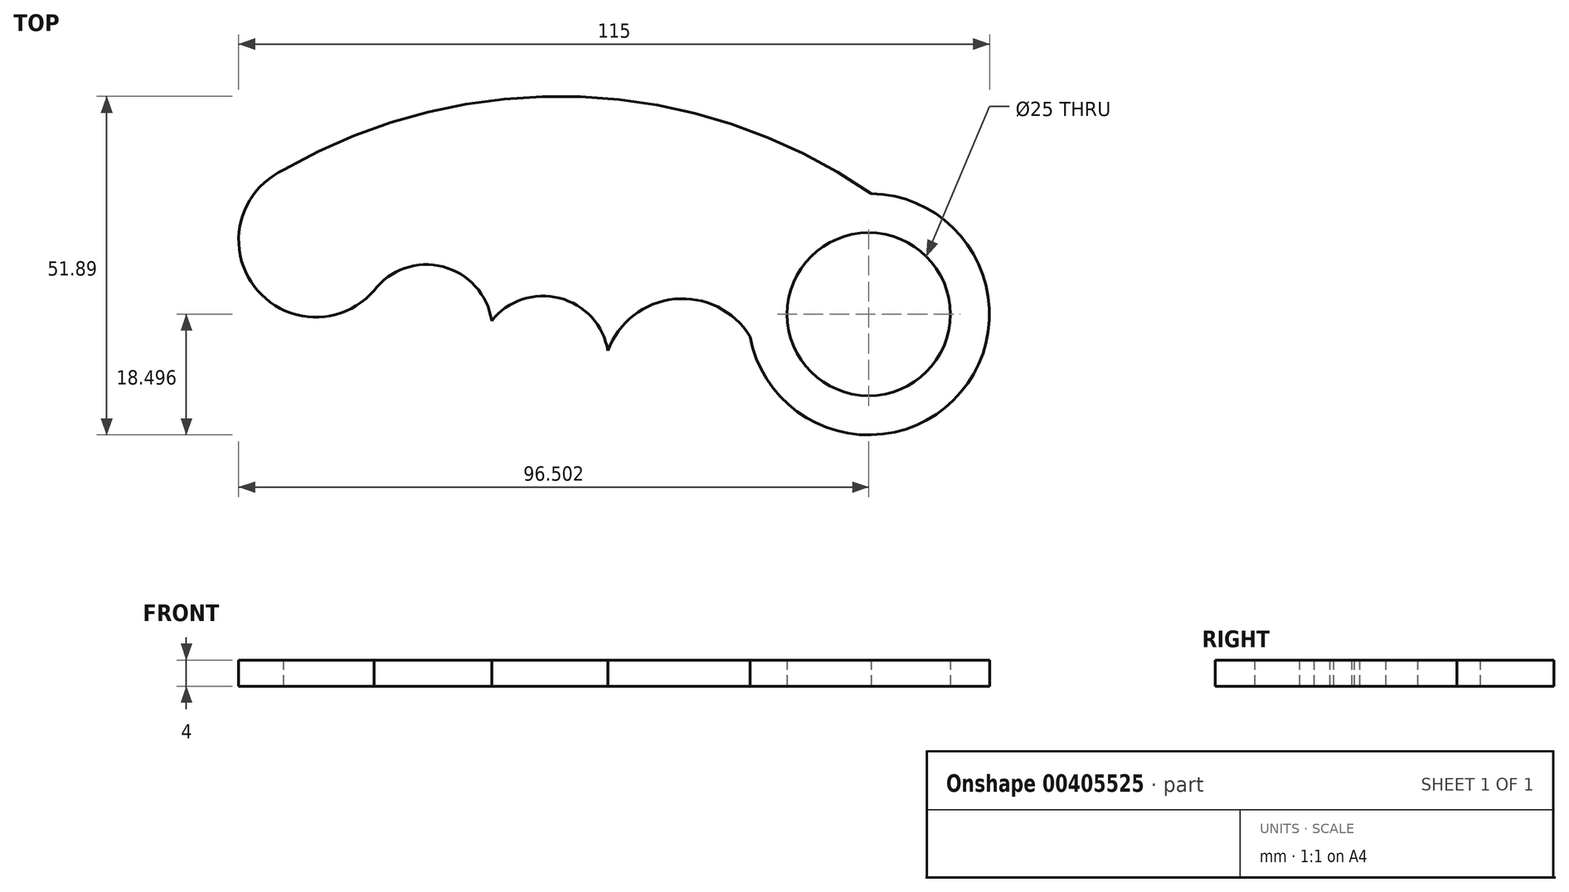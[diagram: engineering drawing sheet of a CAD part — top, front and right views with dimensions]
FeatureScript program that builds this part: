
annotation { "Feature Type Name" : "Feature", "Feature Type Description" : "" }
export const myFeature = defineFeature(function(context is Context, id is Id, definition is map)
    precondition{}
    {
        {
            var Q0;
            Q0=qCreatedBy(makeId("Top.planeOp"),FACE);
            var sketch = newSketch(context, id + "F0", { "sketchPlane" : qUnion([Q0])});
            skCircle(sketch, "E0", {"center": v(47.5, -8.81) * mm, "radius": 12.5 * mm});
            skCircle(sketch, "E1", {"center": v(47.5, -8.81) * mm, "radius": 18.5 * mm});
            skSolve(sketch);
        }
        {
            var Q0;
            Q0 = qSketchRegion(id + "F0", true);
            extrude(context, id + "F1", {"entities" : qUnion([Q0]), "depth" : 4 * mm});
        }
        {
            var Q0;
            Q0=qCreatedBy(makeId("Top.planeOp"),FACE);
            var sketch = newSketch(context, id + "F2", { "sketchPlane" : qUnion([Q0])});
            skArc(sketch, "E2", {"start": v(47.87, 9.68) * mm, "mid": v(3.39, 24.51) * mm, "end": v(-42.14, 13.29) * mm});
            skArc(sketch, "E3", {"start": v(47.87, 9.68) * mm, "mid": v(34.94, -0.97) * mm, "end": v(31.05, -17.27) * mm});
            skArc(sketch, "E4", {"start": v(31.05, -17.27) * mm, "mid": v(20.43, -6.52) * mm, "end": v(7.55, -14.42) * mm});
            skArc(sketch, "E5", {"start": v(7.55, -14.42) * mm, "mid": v(0.15, -6.34) * mm, "end": v(-10.25, -9.8) * mm});
            skArc(sketch, "E6", {"start": v(-10.25, -9.8) * mm, "mid": v(-17.74, -1.52) * mm, "end": v(-28.28, -5.18) * mm});
            skArc(sketch, "E7", {"start": v(-42.14, 13.29) * mm, "mid": v(-46.64, -4.53) * mm, "end": v(-28.28, -5.18) * mm});
            skSolve(sketch);
        }
        {
            var Q0;
            Q0 = qSketchRegion(id + "F2", true);
            var Q1;
            Q1=makeQuery(id+"F1.opExtrude","CAP_FACE",FACE,{"disambiguationData":[OSD([sQuery(id+"F0.wireOp",EDGE,"E0"),sQuery(id+"F0.wireOp",EDGE,"E1")])],"isStart":false});
            extrude(context, id + "F3", {"entities" : qUnion([Q0]), "operationType" : NewBodyOperationType.ADD, "endBound" : BoundingType.UP_TO_SURFACE, "endBoundEntityFace" : qUnion([Q1]), "depth" : 25 * mm});
        }
    });
